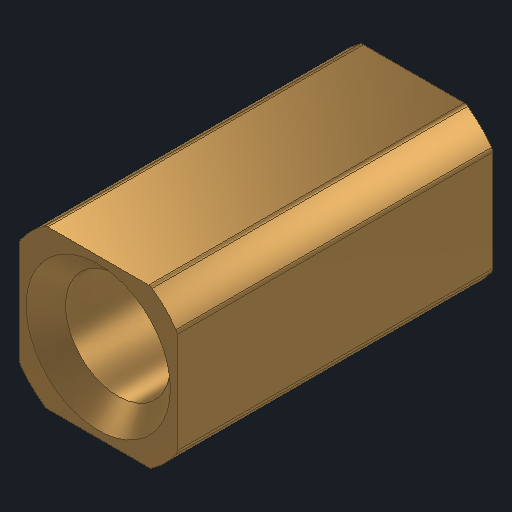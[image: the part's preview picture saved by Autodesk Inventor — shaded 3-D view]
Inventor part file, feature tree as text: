
AUTODESK INVENTOR PART (.ipt)
format: ipt  version: 2024 (Build 280153000, 153)  size: 176,640 bytes
history: native  units: in
note: dims shown in document units (in); Inventor stores cm internally (conversion verified against a paired STEP export)
features: extrude x2, fillet x1, chamfer x1
ambient origin geometry x8: Origin, YZ Plane, XZ Plane, XY Plane, X Axis, Y Axis, Z Axis, Center Point
bodies: Solid1 (feature_tree)
feature tree (4):
  extrude  "Extrusion1"  Depth=0.3in
  extrude  "Extrusion2"  Depth=0.25in
  fillet  "Fillet1"  Radius=0.5in
  chamfer  "Chamfer1"  Distance=0.166in
